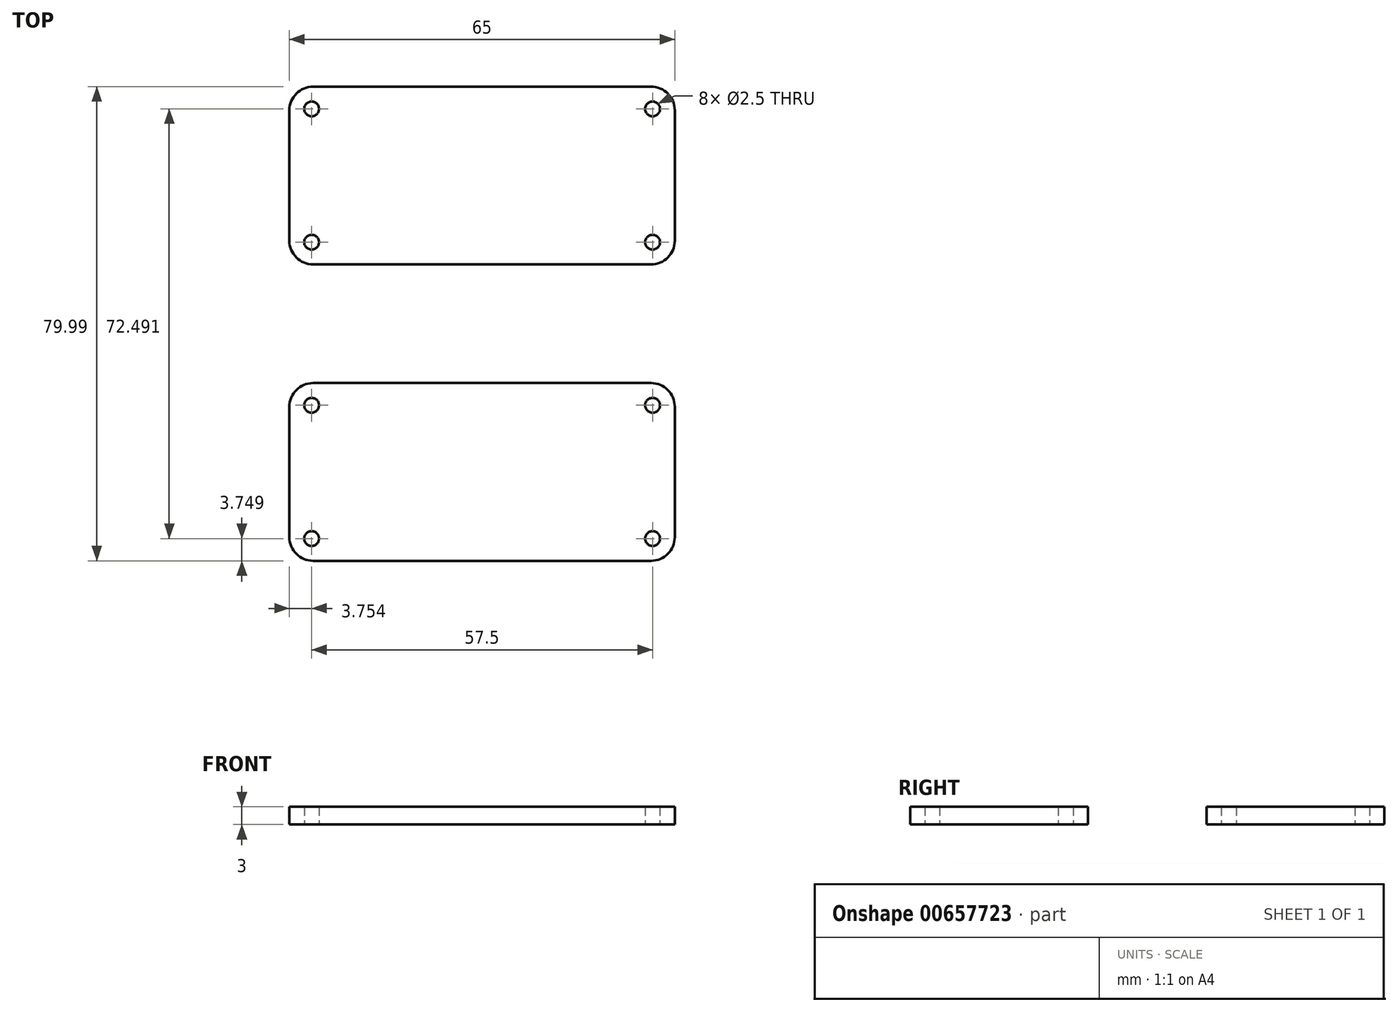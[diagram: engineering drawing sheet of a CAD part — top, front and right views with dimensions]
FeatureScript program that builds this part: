
annotation { "Feature Type Name" : "Feature", "Feature Type Description" : "" }
export const myFeature = defineFeature(function(context is Context, id is Id, definition is map)
    precondition{}
    {
        {
            var Q0;
            Q0=qCreatedBy(makeId("Top.planeOp"),FACE);
            var sketch = newSketch(context, id + "F0", { "sketchPlane" : qUnion([Q0])});
            skLineSegment(sketch, "E0.bottom", {"start": v(-29.92, 16.1) * mm, "end": v(27.08, 16.1) * mm});
            skLineSegment(sketch, "E0.top", {"start": v(-29.92, -13.88) * mm, "end": v(27.08, -13.88) * mm});
            skLineSegment(sketch, "E0.left", {"start": v(-33.92, 12.1) * mm, "end": v(-33.92, -9.88) * mm});
            skLineSegment(sketch, "E0.right", {"start": v(31.08, 12.1) * mm, "end": v(31.08, -9.88) * mm});
            skPoint(sketch, "E1.visualSharp", {"position": v(-33.92, 16.1) * mm});
            skArc(sketch, "E1.filletArc", {"start": v(-29.92, 16.1) * mm, "mid": v(-32.74, 14.94) * mm, "end": v(-33.92, 12.1) * mm});
            skPoint(sketch, "E2.visualSharp", {"position": v(31.08, 16.1) * mm});
            skArc(sketch, "E2.filletArc", {"start": v(31.08, 12.1) * mm, "mid": v(29.91, 14.94) * mm, "end": v(27.08, 16.1) * mm});
            skPoint(sketch, "E3.visualSharp", {"position": v(31.08, -13.88) * mm});
            skArc(sketch, "E3.filletArc", {"start": v(27.08, -13.88) * mm, "mid": v(29.91, -12.7) * mm, "end": v(31.08, -9.88) * mm});
            skPoint(sketch, "E4.visualSharp", {"position": v(-33.92, -13.88) * mm});
            skArc(sketch, "E4.filletArc", {"start": v(-33.92, -9.88) * mm, "mid": v(-32.74, -12.7) * mm, "end": v(-29.92, -13.88) * mm});
            skCircle(sketch, "E5", {"center": v(-30.17, -10.13) * mm, "radius": 1.25 * mm});
            skCircle(sketch, "E6", {"center": v(-30.17, 12.36) * mm, "radius": 1.25 * mm});
            skCircle(sketch, "E7", {"center": v(27.33, 12.36) * mm, "radius": 1.25 * mm});
            skCircle(sketch, "E8", {"center": v(27.33, -10.13) * mm, "radius": 1.25 * mm});
            skSolve(sketch);
        }
        {
            var Q0;
            Q0=makeQuery(id+"F0.imprint","IMPRINT",FACE,{"disambiguationData":[TD([[makeQuery(id+"F0.imprint","IMPRINT",EDGE,{"derivedFrom":sQuery(id+"F0.wireOp",EDGE,"E0.bottom")}),-1.0]])]});
            extrude(context, id + "F1", {"entities" : qUnion([Q0]), "depth" : 3 * mm, "offsetDistance" : 25 * mm});
        }
        {
            var Q0;
            Q0=makeQuery(id+"F1.opExtrude","SWEPT_BODY",BODY,{"disambiguationData":[OSD([sQuery(id+"F0.wireOp",EDGE,"E0.bottom"),sQuery(id+"F0.wireOp",EDGE,"E0.top"),sQuery(id+"F0.wireOp",EDGE,"E0.left"),sQuery(id+"F0.wireOp",EDGE,"E0.right"),sQuery(id+"F0.wireOp",EDGE,"E1.filletArc"),sQuery(id+"F0.wireOp",EDGE,"E2.filletArc"),sQuery(id+"F0.wireOp",EDGE,"E3.filletArc"),sQuery(id+"F0.wireOp",EDGE,"E4.filletArc"),sQuery(id+"F0.wireOp",EDGE,"E5"),sQuery(id+"F0.wireOp",EDGE,"E6"),sQuery(id+"F0.wireOp",EDGE,"E7"),sQuery(id+"F0.wireOp",EDGE,"E8")])]});
            transform(context, id + "F2", {"entities" : qUnion([Q0]), "transformType" : TransformType.TRANSLATION_3D, "dx" : 0 * mm, "dy" : 50 * mm, "dz" : 0 * mm, "makeCopy" : true});
        }
    });
